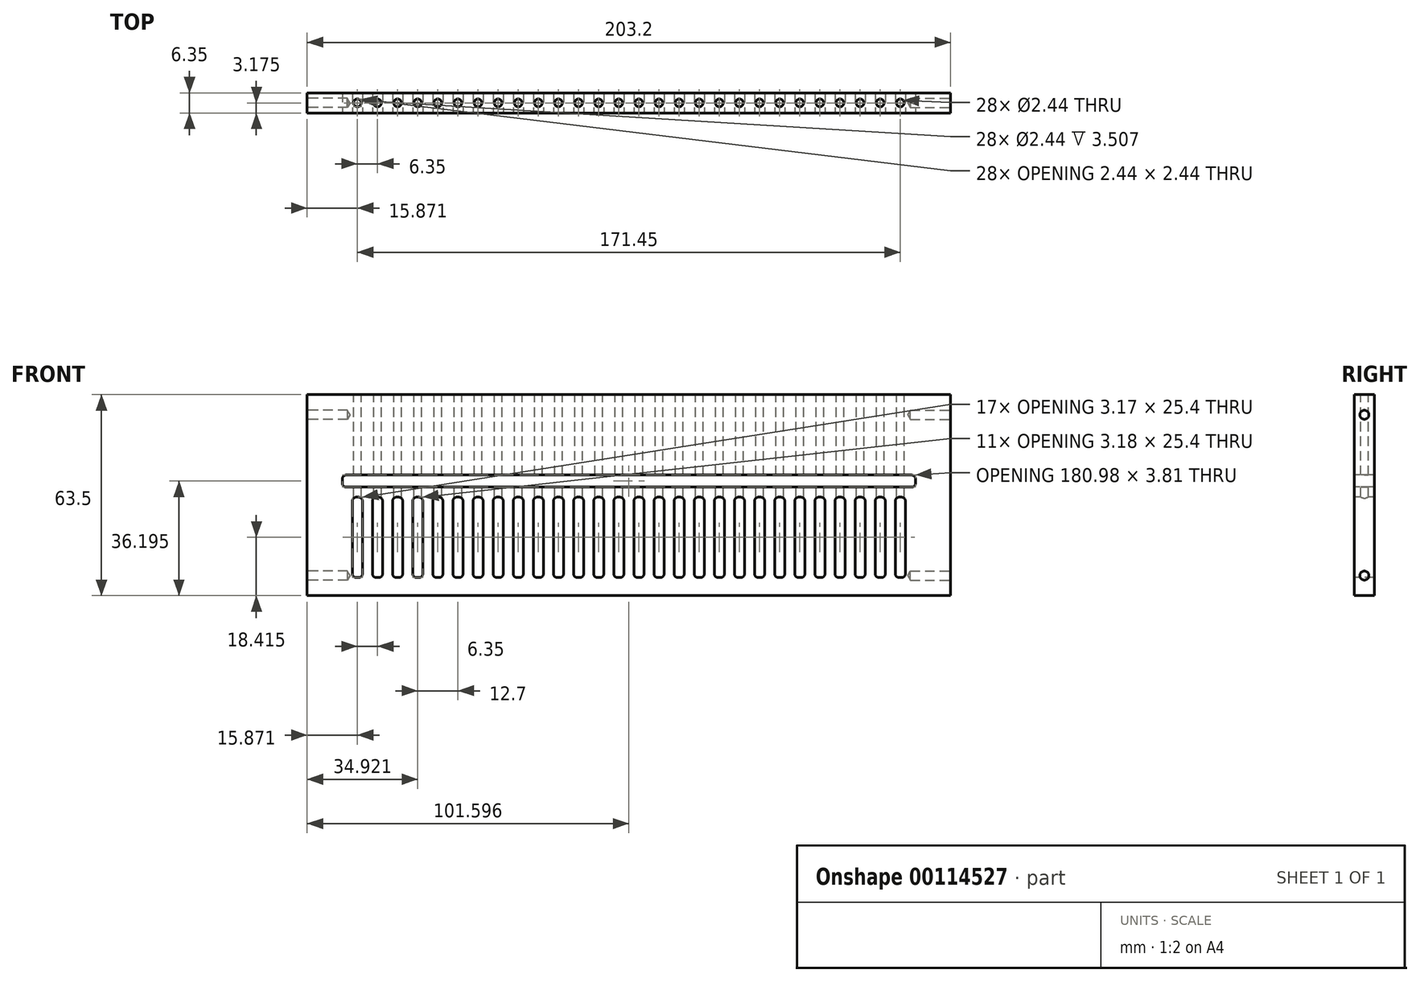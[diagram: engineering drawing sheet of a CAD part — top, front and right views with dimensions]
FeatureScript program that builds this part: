
annotation { "Feature Type Name" : "Feature", "Feature Type Description" : "" }
export const myFeature = defineFeature(function(context is Context, id is Id, definition is map)
    precondition{}
    {
        {
            var Q0;
            Q0=qCreatedBy(makeId("Top.planeOp"),FACE);
            var sketch = newSketch(context, id + "F0", { "sketchPlane" : qUnion([Q0])});
            skLineSegment(sketch, "E0.bottom", {"start": v(-24.78, 0) * mm, "end": v(178.42, 0) * mm});
            skLineSegment(sketch, "E0.top", {"start": v(-24.78, 6.35) * mm, "end": v(178.42, 6.35) * mm});
            skLineSegment(sketch, "E0.left", {"start": v(-24.78, 0) * mm, "end": v(-24.78, 6.35) * mm});
            skLineSegment(sketch, "E0.right", {"start": v(178.42, 0) * mm, "end": v(178.42, 6.35) * mm});
            skSolve(sketch);
        }
        {
            var Q0;
            Q0 = qSketchRegion(id + "F0", true);
            extrude(context, id + "F1", {"entities" : qUnion([Q0]), "depth" : 63.5 * mm});
        }
        {
            var Q0;
            Q0=makeQuery(id+"F1.opExtrude","CAP_FACE",FACE,{"disambiguationData":[OSD([sQuery(id+"F0.wireOp",EDGE,"E0.bottom"),sQuery(id+"F0.wireOp",EDGE,"E0.top"),sQuery(id+"F0.wireOp",EDGE,"E0.left"),sQuery(id+"F0.wireOp",EDGE,"E0.right")])],"isStart":false});
            var sketch = newSketch(context, id + "F2", { "sketchPlane" : qUnion([Q0])});
            skCircle(sketch, "E1", {"center": v(-8.9, 3.18) * mm, "radius": 1.22 * mm});
            skCircle(sketch, "E2.1.0.0", {"center": v(-2.56, 3.18) * mm, "radius": 1.22 * mm});
            skCircle(sketch, "E2.2.0.0", {"center": v(3.8, 3.18) * mm, "radius": 1.22 * mm});
            skCircle(sketch, "E2.3.0.0", {"center": v(10.14, 3.18) * mm, "radius": 1.22 * mm});
            skCircle(sketch, "E2.4.0.0", {"center": v(16.5, 3.18) * mm, "radius": 1.22 * mm});
            skCircle(sketch, "E2.5.0.0", {"center": v(22.84, 3.18) * mm, "radius": 1.22 * mm});
            skCircle(sketch, "E2.6.0.0", {"center": v(29.2, 3.18) * mm, "radius": 1.22 * mm});
            skCircle(sketch, "E2.7.0.0", {"center": v(35.54, 3.18) * mm, "radius": 1.22 * mm});
            skCircle(sketch, "E2.8.0.0", {"center": v(41.9, 3.18) * mm, "radius": 1.22 * mm});
            skCircle(sketch, "E2.9.0.0", {"center": v(48.24, 3.18) * mm, "radius": 1.22 * mm});
            skCircle(sketch, "E2.10.0.0", {"center": v(54.6, 3.18) * mm, "radius": 1.22 * mm});
            skCircle(sketch, "E2.11.0.0", {"center": v(60.94, 3.18) * mm, "radius": 1.22 * mm});
            skCircle(sketch, "E2.12.0.0", {"center": v(67.3, 3.18) * mm, "radius": 1.22 * mm});
            skCircle(sketch, "E2.13.0.0", {"center": v(73.64, 3.18) * mm, "radius": 1.22 * mm});
            skCircle(sketch, "E2.14.0.0", {"center": v(80, 3.18) * mm, "radius": 1.22 * mm});
            skCircle(sketch, "E2.15.0.0", {"center": v(86.34, 3.18) * mm, "radius": 1.22 * mm});
            skCircle(sketch, "E2.16.0.0", {"center": v(92.7, 3.18) * mm, "radius": 1.22 * mm});
            skCircle(sketch, "E2.17.0.0", {"center": v(99.04, 3.18) * mm, "radius": 1.22 * mm});
            skCircle(sketch, "E2.18.0.0", {"center": v(105.4, 3.18) * mm, "radius": 1.22 * mm});
            skCircle(sketch, "E2.19.0.0", {"center": v(111.74, 3.18) * mm, "radius": 1.22 * mm});
            skCircle(sketch, "E2.20.0.0", {"center": v(118.1, 3.18) * mm, "radius": 1.22 * mm});
            skCircle(sketch, "E2.21.0.0", {"center": v(124.44, 3.18) * mm, "radius": 1.22 * mm});
            skCircle(sketch, "E2.22.0.0", {"center": v(130.8, 3.18) * mm, "radius": 1.22 * mm});
            skCircle(sketch, "E2.23.0.0", {"center": v(137.14, 3.18) * mm, "radius": 1.22 * mm});
            skCircle(sketch, "E2.24.0.0", {"center": v(143.5, 3.18) * mm, "radius": 1.22 * mm});
            skCircle(sketch, "E2.25.0.0", {"center": v(149.84, 3.18) * mm, "radius": 1.22 * mm});
            skCircle(sketch, "E2.26.0.0", {"center": v(156.2, 3.18) * mm, "radius": 1.22 * mm});
            skCircle(sketch, "E2.27.0.0", {"center": v(162.54, 3.18) * mm, "radius": 1.22 * mm});
            skLineSegment(sketch, "E2.direction1", {"start": v(-8.9, 3.18) * mm, "end": v(-2.56, 3.18) * mm, "construction": true});
            skSolve(sketch);
        }
        {
            var Q0;
            Q0 = qSketchRegion(id + "F2", true);
            extrude(context, id + "F3", {"entities" : qUnion([Q0]), "operationType" : NewBodyOperationType.REMOVE, "oppositeDirection" : true, "depth" : 38.1 * mm});
        }
        {
            var Q0;
            Q0=makeQuery(id+"F1.opExtrude","SWEPT_FACE",FACE,{"disambiguationData":[OSD([sQuery(id+"F0.wireOp",EDGE,"E0.bottom")])]});
            var sketch = newSketch(context, id + "F4", { "sketchPlane" : qUnion([Q0])});
            skLineSegment(sketch, "E3.bottom", {"start": v(-12.48, 38.1) * mm, "end": v(166.11, 38.1) * mm});
            skLineSegment(sketch, "E3.top", {"start": v(-12.48, 34.29) * mm, "end": v(166.11, 34.29) * mm});
            skLineSegment(sketch, "E3.left", {"start": v(-13.67, 36.9) * mm, "end": v(-13.67, 35.48) * mm});
            skLineSegment(sketch, "E3.right", {"start": v(167.3, 36.9) * mm, "end": v(167.3, 35.48) * mm});
            skPoint(sketch, "E4.visualSharp", {"position": v(-13.67, 38.1) * mm});
            skArc(sketch, "E4.filletArc", {"start": v(-12.48, 38.1) * mm, "mid": v(-13.32, 37.75) * mm, "end": v(-13.67, 36.9) * mm});
            skPoint(sketch, "E5.visualSharp", {"position": v(-13.67, 34.29) * mm});
            skArc(sketch, "E5.filletArc", {"start": v(-13.67, 35.48) * mm, "mid": v(-13.32, 34.64) * mm, "end": v(-12.48, 34.3) * mm});
            skPoint(sketch, "E6.visualSharp", {"position": v(167.3, 38.1) * mm});
            skArc(sketch, "E6.filletArc", {"start": v(167.3, 36.9) * mm, "mid": v(166.95, 37.75) * mm, "end": v(166.11, 38.1) * mm});
            skPoint(sketch, "E7.visualSharp", {"position": v(167.3, 34.29) * mm});
            skArc(sketch, "E7.filletArc", {"start": v(166.11, 34.29) * mm, "mid": v(166.95, 34.64) * mm, "end": v(167.3, 35.48) * mm});
            skLineSegment(sketch, "E8.bottom", {"start": v(-9.3, 31.12) * mm, "end": v(-8.51, 31.12) * mm});
            skLineSegment(sketch, "E8.top", {"start": v(-9.3, 5.71) * mm, "end": v(-8.51, 5.71) * mm});
            skLineSegment(sketch, "E8.left", {"start": v(-10.5, 29.92) * mm, "end": v(-10.5, 6.9) * mm});
            skLineSegment(sketch, "E8.right", {"start": v(-7.32, 29.92) * mm, "end": v(-7.32, 6.9) * mm});
            skPoint(sketch, "E9.visualSharp", {"position": v(-10.5, 31.12) * mm});
            skArc(sketch, "E9.filletArc", {"start": v(-9.3, 31.12) * mm, "mid": v(-10.15, 30.77) * mm, "end": v(-10.5, 29.92) * mm});
            skPoint(sketch, "E10.visualSharp", {"position": v(-7.32, 31.12) * mm});
            skArc(sketch, "E10.filletArc", {"start": v(-7.32, 29.92) * mm, "mid": v(-7.67, 30.77) * mm, "end": v(-8.51, 31.12) * mm});
            skPoint(sketch, "E11.visualSharp", {"position": v(-10.5, 5.71) * mm});
            skArc(sketch, "E11.filletArc", {"start": v(-10.5, 6.9) * mm, "mid": v(-10.15, 6.06) * mm, "end": v(-9.3, 5.71) * mm});
            skPoint(sketch, "E12.visualSharp", {"position": v(-7.32, 5.71) * mm});
            skArc(sketch, "E12.filletArc", {"start": v(-8.51, 5.71) * mm, "mid": v(-7.67, 6.06) * mm, "end": v(-7.32, 6.9) * mm});
            skPoint(sketch, "E13.1.0.0", {"position": v(-0.97, 31.12) * mm});
            skPoint(sketch, "E13.1.0.1", {"position": v(-4.15, 5.71) * mm});
            skPoint(sketch, "E13.1.0.2", {"position": v(-4.15, 31.12) * mm});
            skPoint(sketch, "E13.1.0.3", {"position": v(-0.97, 5.71) * mm});
            skLineSegment(sketch, "E13.1.0.4", {"start": v(-0.97, 29.92) * mm, "end": v(-0.97, 6.9) * mm});
            skLineSegment(sketch, "E13.1.0.5", {"start": v(-4.15, 29.92) * mm, "end": v(-4.15, 6.9) * mm});
            skArc(sketch, "E13.1.0.6", {"start": v(-2.96, 31.12) * mm, "mid": v(-3.8, 30.77) * mm, "end": v(-4.15, 29.92) * mm});
            skArc(sketch, "E13.1.0.7", {"start": v(-0.97, 29.92) * mm, "mid": v(-1.32, 30.77) * mm, "end": v(-2.16, 31.12) * mm});
            skArc(sketch, "E13.1.0.8", {"start": v(-4.15, 6.9) * mm, "mid": v(-3.8, 6.06) * mm, "end": v(-2.96, 5.71) * mm});
            skArc(sketch, "E13.1.0.9", {"start": v(-2.16, 5.71) * mm, "mid": v(-1.32, 6.06) * mm, "end": v(-0.97, 6.9) * mm});
            skLineSegment(sketch, "E13.1.0.10", {"start": v(-2.96, 5.71) * mm, "end": v(-2.16, 5.71) * mm});
            skLineSegment(sketch, "E13.1.0.11", {"start": v(-2.96, 31.12) * mm, "end": v(-2.16, 31.12) * mm});
            skPoint(sketch, "E13.2.0.0", {"position": v(5.38, 31.12) * mm});
            skPoint(sketch, "E13.2.0.1", {"position": v(2.2, 5.71) * mm});
            skPoint(sketch, "E13.2.0.2", {"position": v(2.2, 31.12) * mm});
            skPoint(sketch, "E13.2.0.3", {"position": v(5.38, 5.71) * mm});
            skLineSegment(sketch, "E13.2.0.4", {"start": v(5.38, 29.92) * mm, "end": v(5.38, 6.9) * mm});
            skLineSegment(sketch, "E13.2.0.5", {"start": v(2.2, 29.92) * mm, "end": v(2.2, 6.9) * mm});
            skArc(sketch, "E13.2.0.6", {"start": v(3.4, 31.12) * mm, "mid": v(2.55, 30.77) * mm, "end": v(2.2, 29.92) * mm});
            skArc(sketch, "E13.2.0.7", {"start": v(5.38, 29.92) * mm, "mid": v(5.03, 30.77) * mm, "end": v(4.19, 31.12) * mm});
            skArc(sketch, "E13.2.0.8", {"start": v(2.2, 6.9) * mm, "mid": v(2.55, 6.06) * mm, "end": v(3.4, 5.71) * mm});
            skArc(sketch, "E13.2.0.9", {"start": v(4.19, 5.71) * mm, "mid": v(5.03, 6.06) * mm, "end": v(5.38, 6.9) * mm});
            skLineSegment(sketch, "E13.2.0.10", {"start": v(3.4, 5.71) * mm, "end": v(4.19, 5.71) * mm});
            skLineSegment(sketch, "E13.2.0.11", {"start": v(3.4, 31.12) * mm, "end": v(4.19, 31.12) * mm});
            skPoint(sketch, "E13.3.0.0", {"position": v(11.73, 31.12) * mm});
            skPoint(sketch, "E13.3.0.1", {"position": v(8.55, 5.71) * mm});
            skPoint(sketch, "E13.3.0.2", {"position": v(8.55, 31.12) * mm});
            skPoint(sketch, "E13.3.0.3", {"position": v(11.73, 5.71) * mm});
            skLineSegment(sketch, "E13.3.0.4", {"start": v(11.73, 29.92) * mm, "end": v(11.73, 6.9) * mm});
            skLineSegment(sketch, "E13.3.0.5", {"start": v(8.55, 29.92) * mm, "end": v(8.55, 6.9) * mm});
            skArc(sketch, "E13.3.0.6", {"start": v(9.74, 31.12) * mm, "mid": v(8.9, 30.77) * mm, "end": v(8.55, 29.92) * mm});
            skArc(sketch, "E13.3.0.7", {"start": v(11.73, 29.92) * mm, "mid": v(11.38, 30.77) * mm, "end": v(10.54, 31.12) * mm});
            skArc(sketch, "E13.3.0.8", {"start": v(8.55, 6.9) * mm, "mid": v(8.9, 6.06) * mm, "end": v(9.74, 5.71) * mm});
            skArc(sketch, "E13.3.0.9", {"start": v(10.54, 5.71) * mm, "mid": v(11.38, 6.06) * mm, "end": v(11.73, 6.9) * mm});
            skLineSegment(sketch, "E13.3.0.10", {"start": v(9.74, 5.71) * mm, "end": v(10.54, 5.71) * mm});
            skLineSegment(sketch, "E13.3.0.11", {"start": v(9.74, 31.11) * mm, "end": v(10.54, 31.11) * mm});
            skPoint(sketch, "E13.4.0.0", {"position": v(18.08, 31.12) * mm});
            skPoint(sketch, "E13.4.0.1", {"position": v(14.9, 5.71) * mm});
            skPoint(sketch, "E13.4.0.2", {"position": v(14.9, 31.12) * mm});
            skPoint(sketch, "E13.4.0.3", {"position": v(18.08, 5.71) * mm});
            skLineSegment(sketch, "E13.4.0.4", {"start": v(18.08, 29.92) * mm, "end": v(18.08, 6.9) * mm});
            skLineSegment(sketch, "E13.4.0.5", {"start": v(14.9, 29.92) * mm, "end": v(14.9, 6.9) * mm});
            skArc(sketch, "E13.4.0.6", {"start": v(16.1, 31.12) * mm, "mid": v(15.25, 30.77) * mm, "end": v(14.9, 29.92) * mm});
            skArc(sketch, "E13.4.0.7", {"start": v(18.08, 29.92) * mm, "mid": v(17.73, 30.77) * mm, "end": v(16.89, 31.12) * mm});
            skArc(sketch, "E13.4.0.8", {"start": v(14.9, 6.9) * mm, "mid": v(15.25, 6.06) * mm, "end": v(16.1, 5.71) * mm});
            skArc(sketch, "E13.4.0.9", {"start": v(16.89, 5.71) * mm, "mid": v(17.73, 6.06) * mm, "end": v(18.08, 6.9) * mm});
            skLineSegment(sketch, "E13.4.0.10", {"start": v(16.1, 5.71) * mm, "end": v(16.89, 5.71) * mm});
            skLineSegment(sketch, "E13.4.0.11", {"start": v(16.1, 31.11) * mm, "end": v(16.89, 31.11) * mm});
            skPoint(sketch, "E13.5.0.0", {"position": v(24.43, 31.12) * mm});
            skPoint(sketch, "E13.5.0.1", {"position": v(21.25, 5.71) * mm});
            skPoint(sketch, "E13.5.0.2", {"position": v(21.25, 31.12) * mm});
            skPoint(sketch, "E13.5.0.3", {"position": v(24.43, 5.71) * mm});
            skLineSegment(sketch, "E13.5.0.4", {"start": v(24.43, 29.92) * mm, "end": v(24.43, 6.9) * mm});
            skLineSegment(sketch, "E13.5.0.5", {"start": v(21.25, 29.92) * mm, "end": v(21.25, 6.9) * mm});
            skArc(sketch, "E13.5.0.6", {"start": v(22.44, 31.12) * mm, "mid": v(21.6, 30.77) * mm, "end": v(21.25, 29.92) * mm});
            skArc(sketch, "E13.5.0.7", {"start": v(24.43, 29.92) * mm, "mid": v(24.08, 30.77) * mm, "end": v(23.24, 31.12) * mm});
            skArc(sketch, "E13.5.0.8", {"start": v(21.25, 6.9) * mm, "mid": v(21.6, 6.06) * mm, "end": v(22.44, 5.71) * mm});
            skArc(sketch, "E13.5.0.9", {"start": v(23.24, 5.71) * mm, "mid": v(24.08, 6.06) * mm, "end": v(24.43, 6.9) * mm});
            skLineSegment(sketch, "E13.5.0.10", {"start": v(22.44, 5.71) * mm, "end": v(23.24, 5.71) * mm});
            skLineSegment(sketch, "E13.5.0.11", {"start": v(22.44, 31.11) * mm, "end": v(23.24, 31.11) * mm});
            skPoint(sketch, "E13.6.0.0", {"position": v(30.78, 31.12) * mm});
            skPoint(sketch, "E13.6.0.1", {"position": v(27.6, 5.71) * mm});
            skPoint(sketch, "E13.6.0.2", {"position": v(27.6, 31.12) * mm});
            skPoint(sketch, "E13.6.0.3", {"position": v(30.78, 5.71) * mm});
            skLineSegment(sketch, "E13.6.0.4", {"start": v(30.78, 29.92) * mm, "end": v(30.78, 6.9) * mm});
            skLineSegment(sketch, "E13.6.0.5", {"start": v(27.6, 29.92) * mm, "end": v(27.6, 6.9) * mm});
            skArc(sketch, "E13.6.0.6", {"start": v(28.8, 31.12) * mm, "mid": v(27.95, 30.77) * mm, "end": v(27.6, 29.92) * mm});
            skArc(sketch, "E13.6.0.7", {"start": v(30.78, 29.92) * mm, "mid": v(30.43, 30.77) * mm, "end": v(29.59, 31.12) * mm});
            skArc(sketch, "E13.6.0.8", {"start": v(27.6, 6.9) * mm, "mid": v(27.95, 6.06) * mm, "end": v(28.8, 5.71) * mm});
            skArc(sketch, "E13.6.0.9", {"start": v(29.59, 5.71) * mm, "mid": v(30.43, 6.06) * mm, "end": v(30.78, 6.9) * mm});
            skLineSegment(sketch, "E13.6.0.10", {"start": v(28.8, 5.71) * mm, "end": v(29.59, 5.71) * mm});
            skLineSegment(sketch, "E13.6.0.11", {"start": v(28.8, 31.11) * mm, "end": v(29.59, 31.11) * mm});
            skPoint(sketch, "E13.7.0.0", {"position": v(37.13, 31.12) * mm});
            skPoint(sketch, "E13.7.0.1", {"position": v(33.95, 5.71) * mm});
            skPoint(sketch, "E13.7.0.2", {"position": v(33.95, 31.12) * mm});
            skPoint(sketch, "E13.7.0.3", {"position": v(37.13, 5.71) * mm});
            skLineSegment(sketch, "E13.7.0.4", {"start": v(37.13, 29.92) * mm, "end": v(37.13, 6.9) * mm});
            skLineSegment(sketch, "E13.7.0.5", {"start": v(33.95, 29.92) * mm, "end": v(33.95, 6.9) * mm});
            skArc(sketch, "E13.7.0.6", {"start": v(35.14, 31.12) * mm, "mid": v(34.3, 30.77) * mm, "end": v(33.95, 29.92) * mm});
            skArc(sketch, "E13.7.0.7", {"start": v(37.13, 29.92) * mm, "mid": v(36.78, 30.77) * mm, "end": v(35.94, 31.12) * mm});
            skArc(sketch, "E13.7.0.8", {"start": v(33.95, 6.9) * mm, "mid": v(34.3, 6.06) * mm, "end": v(35.14, 5.71) * mm});
            skArc(sketch, "E13.7.0.9", {"start": v(35.94, 5.71) * mm, "mid": v(36.78, 6.06) * mm, "end": v(37.13, 6.9) * mm});
            skLineSegment(sketch, "E13.7.0.10", {"start": v(35.14, 5.71) * mm, "end": v(35.94, 5.71) * mm});
            skLineSegment(sketch, "E13.7.0.11", {"start": v(35.14, 31.11) * mm, "end": v(35.94, 31.11) * mm});
            skPoint(sketch, "E13.8.0.0", {"position": v(43.48, 31.12) * mm});
            skPoint(sketch, "E13.8.0.1", {"position": v(40.3, 5.71) * mm});
            skPoint(sketch, "E13.8.0.2", {"position": v(40.3, 31.12) * mm});
            skPoint(sketch, "E13.8.0.3", {"position": v(43.48, 5.71) * mm});
            skLineSegment(sketch, "E13.8.0.4", {"start": v(43.48, 29.92) * mm, "end": v(43.48, 6.9) * mm});
            skLineSegment(sketch, "E13.8.0.5", {"start": v(40.3, 29.92) * mm, "end": v(40.3, 6.9) * mm});
            skArc(sketch, "E13.8.0.6", {"start": v(41.5, 31.12) * mm, "mid": v(40.65, 30.77) * mm, "end": v(40.3, 29.92) * mm});
            skArc(sketch, "E13.8.0.7", {"start": v(43.48, 29.92) * mm, "mid": v(43.13, 30.77) * mm, "end": v(42.29, 31.12) * mm});
            skArc(sketch, "E13.8.0.8", {"start": v(40.3, 6.9) * mm, "mid": v(40.65, 6.06) * mm, "end": v(41.5, 5.71) * mm});
            skArc(sketch, "E13.8.0.9", {"start": v(42.29, 5.71) * mm, "mid": v(43.13, 6.06) * mm, "end": v(43.48, 6.9) * mm});
            skLineSegment(sketch, "E13.8.0.10", {"start": v(41.5, 5.71) * mm, "end": v(42.29, 5.71) * mm});
            skLineSegment(sketch, "E13.8.0.11", {"start": v(41.5, 31.11) * mm, "end": v(42.29, 31.11) * mm});
            skPoint(sketch, "E13.9.0.0", {"position": v(49.83, 31.12) * mm});
            skPoint(sketch, "E13.9.0.1", {"position": v(46.65, 5.71) * mm});
            skPoint(sketch, "E13.9.0.2", {"position": v(46.65, 31.12) * mm});
            skPoint(sketch, "E13.9.0.3", {"position": v(49.83, 5.71) * mm});
            skLineSegment(sketch, "E13.9.0.4", {"start": v(49.83, 29.92) * mm, "end": v(49.83, 6.9) * mm});
            skLineSegment(sketch, "E13.9.0.5", {"start": v(46.65, 29.92) * mm, "end": v(46.65, 6.9) * mm});
            skArc(sketch, "E13.9.0.6", {"start": v(47.84, 31.12) * mm, "mid": v(47, 30.77) * mm, "end": v(46.65, 29.92) * mm});
            skArc(sketch, "E13.9.0.7", {"start": v(49.83, 29.92) * mm, "mid": v(49.48, 30.77) * mm, "end": v(48.64, 31.12) * mm});
            skArc(sketch, "E13.9.0.8", {"start": v(46.65, 6.9) * mm, "mid": v(47, 6.06) * mm, "end": v(47.84, 5.71) * mm});
            skArc(sketch, "E13.9.0.9", {"start": v(48.64, 5.71) * mm, "mid": v(49.48, 6.06) * mm, "end": v(49.83, 6.9) * mm});
            skLineSegment(sketch, "E13.9.0.10", {"start": v(47.84, 5.71) * mm, "end": v(48.64, 5.71) * mm});
            skLineSegment(sketch, "E13.9.0.11", {"start": v(47.84, 31.11) * mm, "end": v(48.64, 31.11) * mm});
            skPoint(sketch, "E13.10.0.0", {"position": v(56.18, 31.12) * mm});
            skPoint(sketch, "E13.10.0.1", {"position": v(53, 5.71) * mm});
            skPoint(sketch, "E13.10.0.2", {"position": v(53, 31.12) * mm});
            skPoint(sketch, "E13.10.0.3", {"position": v(56.18, 5.71) * mm});
            skLineSegment(sketch, "E13.10.0.4", {"start": v(56.18, 29.92) * mm, "end": v(56.18, 6.9) * mm});
            skLineSegment(sketch, "E13.10.0.5", {"start": v(53, 29.92) * mm, "end": v(53, 6.9) * mm});
            skArc(sketch, "E13.10.0.6", {"start": v(54.2, 31.12) * mm, "mid": v(53.35, 30.77) * mm, "end": v(53, 29.92) * mm});
            skArc(sketch, "E13.10.0.7", {"start": v(56.18, 29.92) * mm, "mid": v(55.83, 30.77) * mm, "end": v(54.99, 31.12) * mm});
            skArc(sketch, "E13.10.0.8", {"start": v(53, 6.9) * mm, "mid": v(53.35, 6.06) * mm, "end": v(54.2, 5.71) * mm});
            skArc(sketch, "E13.10.0.9", {"start": v(54.99, 5.71) * mm, "mid": v(55.83, 6.06) * mm, "end": v(56.18, 6.9) * mm});
            skLineSegment(sketch, "E13.10.0.10", {"start": v(54.2, 5.71) * mm, "end": v(54.99, 5.71) * mm});
            skLineSegment(sketch, "E13.10.0.11", {"start": v(54.2, 31.11) * mm, "end": v(54.99, 31.11) * mm});
            skPoint(sketch, "E13.11.0.0", {"position": v(62.53, 31.12) * mm});
            skPoint(sketch, "E13.11.0.1", {"position": v(59.35, 5.71) * mm});
            skPoint(sketch, "E13.11.0.2", {"position": v(59.35, 31.12) * mm});
            skPoint(sketch, "E13.11.0.3", {"position": v(62.53, 5.71) * mm});
            skLineSegment(sketch, "E13.11.0.4", {"start": v(62.53, 29.92) * mm, "end": v(62.53, 6.9) * mm});
            skLineSegment(sketch, "E13.11.0.5", {"start": v(59.35, 29.92) * mm, "end": v(59.35, 6.9) * mm});
            skArc(sketch, "E13.11.0.6", {"start": v(60.54, 31.12) * mm, "mid": v(59.7, 30.77) * mm, "end": v(59.35, 29.92) * mm});
            skArc(sketch, "E13.11.0.7", {"start": v(62.53, 29.92) * mm, "mid": v(62.18, 30.77) * mm, "end": v(61.34, 31.12) * mm});
            skArc(sketch, "E13.11.0.8", {"start": v(59.35, 6.9) * mm, "mid": v(59.7, 6.06) * mm, "end": v(60.54, 5.71) * mm});
            skArc(sketch, "E13.11.0.9", {"start": v(61.34, 5.71) * mm, "mid": v(62.18, 6.06) * mm, "end": v(62.53, 6.9) * mm});
            skLineSegment(sketch, "E13.11.0.10", {"start": v(60.54, 5.71) * mm, "end": v(61.34, 5.71) * mm});
            skLineSegment(sketch, "E13.11.0.11", {"start": v(60.54, 31.11) * mm, "end": v(61.34, 31.11) * mm});
            skPoint(sketch, "E13.12.0.0", {"position": v(68.88, 31.12) * mm});
            skPoint(sketch, "E13.12.0.1", {"position": v(65.7, 5.71) * mm});
            skPoint(sketch, "E13.12.0.2", {"position": v(65.7, 31.12) * mm});
            skPoint(sketch, "E13.12.0.3", {"position": v(68.88, 5.71) * mm});
            skLineSegment(sketch, "E13.12.0.4", {"start": v(68.88, 29.92) * mm, "end": v(68.88, 6.9) * mm});
            skLineSegment(sketch, "E13.12.0.5", {"start": v(65.7, 29.92) * mm, "end": v(65.7, 6.9) * mm});
            skArc(sketch, "E13.12.0.6", {"start": v(66.9, 31.12) * mm, "mid": v(66.05, 30.77) * mm, "end": v(65.7, 29.92) * mm});
            skArc(sketch, "E13.12.0.7", {"start": v(68.88, 29.92) * mm, "mid": v(68.53, 30.77) * mm, "end": v(67.69, 31.12) * mm});
            skArc(sketch, "E13.12.0.8", {"start": v(65.7, 6.9) * mm, "mid": v(66.05, 6.06) * mm, "end": v(66.9, 5.71) * mm});
            skArc(sketch, "E13.12.0.9", {"start": v(67.69, 5.71) * mm, "mid": v(68.53, 6.06) * mm, "end": v(68.88, 6.9) * mm});
            skLineSegment(sketch, "E13.12.0.10", {"start": v(66.9, 5.71) * mm, "end": v(67.69, 5.71) * mm});
            skLineSegment(sketch, "E13.12.0.11", {"start": v(66.9, 31.11) * mm, "end": v(67.69, 31.11) * mm});
            skPoint(sketch, "E13.13.0.0", {"position": v(75.23, 31.12) * mm});
            skPoint(sketch, "E13.13.0.1", {"position": v(72.05, 5.71) * mm});
            skPoint(sketch, "E13.13.0.2", {"position": v(72.05, 31.12) * mm});
            skPoint(sketch, "E13.13.0.3", {"position": v(75.23, 5.71) * mm});
            skLineSegment(sketch, "E13.13.0.4", {"start": v(75.23, 29.92) * mm, "end": v(75.23, 6.9) * mm});
            skLineSegment(sketch, "E13.13.0.5", {"start": v(72.05, 29.92) * mm, "end": v(72.05, 6.9) * mm});
            skArc(sketch, "E13.13.0.6", {"start": v(73.24, 31.12) * mm, "mid": v(72.4, 30.77) * mm, "end": v(72.05, 29.92) * mm});
            skArc(sketch, "E13.13.0.7", {"start": v(75.23, 29.92) * mm, "mid": v(74.88, 30.77) * mm, "end": v(74.04, 31.12) * mm});
            skArc(sketch, "E13.13.0.8", {"start": v(72.05, 6.9) * mm, "mid": v(72.4, 6.06) * mm, "end": v(73.24, 5.71) * mm});
            skArc(sketch, "E13.13.0.9", {"start": v(74.04, 5.71) * mm, "mid": v(74.88, 6.06) * mm, "end": v(75.23, 6.9) * mm});
            skLineSegment(sketch, "E13.13.0.10", {"start": v(73.24, 5.71) * mm, "end": v(74.04, 5.71) * mm});
            skLineSegment(sketch, "E13.13.0.11", {"start": v(73.24, 31.11) * mm, "end": v(74.04, 31.11) * mm});
            skPoint(sketch, "E13.14.0.0", {"position": v(81.58, 31.12) * mm});
            skPoint(sketch, "E13.14.0.1", {"position": v(78.4, 5.71) * mm});
            skPoint(sketch, "E13.14.0.2", {"position": v(78.4, 31.12) * mm});
            skPoint(sketch, "E13.14.0.3", {"position": v(81.58, 5.71) * mm});
            skLineSegment(sketch, "E13.14.0.4", {"start": v(81.58, 29.92) * mm, "end": v(81.58, 6.9) * mm});
            skLineSegment(sketch, "E13.14.0.5", {"start": v(78.4, 29.92) * mm, "end": v(78.4, 6.9) * mm});
            skArc(sketch, "E13.14.0.6", {"start": v(79.6, 31.12) * mm, "mid": v(78.75, 30.77) * mm, "end": v(78.4, 29.92) * mm});
            skArc(sketch, "E13.14.0.7", {"start": v(81.58, 29.92) * mm, "mid": v(81.23, 30.77) * mm, "end": v(80.39, 31.12) * mm});
            skArc(sketch, "E13.14.0.8", {"start": v(78.4, 6.9) * mm, "mid": v(78.75, 6.06) * mm, "end": v(79.6, 5.71) * mm});
            skArc(sketch, "E13.14.0.9", {"start": v(80.39, 5.71) * mm, "mid": v(81.23, 6.06) * mm, "end": v(81.58, 6.9) * mm});
            skLineSegment(sketch, "E13.14.0.10", {"start": v(79.6, 5.71) * mm, "end": v(80.39, 5.71) * mm});
            skLineSegment(sketch, "E13.14.0.11", {"start": v(79.6, 31.11) * mm, "end": v(80.39, 31.11) * mm});
            skPoint(sketch, "E13.15.0.0", {"position": v(87.93, 31.12) * mm});
            skPoint(sketch, "E13.15.0.1", {"position": v(84.75, 5.71) * mm});
            skPoint(sketch, "E13.15.0.2", {"position": v(84.75, 31.12) * mm});
            skPoint(sketch, "E13.15.0.3", {"position": v(87.93, 5.71) * mm});
            skLineSegment(sketch, "E13.15.0.4", {"start": v(87.93, 29.92) * mm, "end": v(87.93, 6.9) * mm});
            skLineSegment(sketch, "E13.15.0.5", {"start": v(84.75, 29.92) * mm, "end": v(84.75, 6.9) * mm});
            skArc(sketch, "E13.15.0.6", {"start": v(85.94, 31.12) * mm, "mid": v(85.1, 30.77) * mm, "end": v(84.75, 29.92) * mm});
            skArc(sketch, "E13.15.0.7", {"start": v(87.93, 29.92) * mm, "mid": v(87.58, 30.77) * mm, "end": v(86.74, 31.12) * mm});
            skArc(sketch, "E13.15.0.8", {"start": v(84.75, 6.9) * mm, "mid": v(85.1, 6.06) * mm, "end": v(85.94, 5.71) * mm});
            skArc(sketch, "E13.15.0.9", {"start": v(86.74, 5.71) * mm, "mid": v(87.58, 6.06) * mm, "end": v(87.93, 6.9) * mm});
            skLineSegment(sketch, "E13.15.0.10", {"start": v(85.94, 5.71) * mm, "end": v(86.74, 5.71) * mm});
            skLineSegment(sketch, "E13.15.0.11", {"start": v(85.94, 31.11) * mm, "end": v(86.74, 31.11) * mm});
            skPoint(sketch, "E13.16.0.0", {"position": v(94.28, 31.12) * mm});
            skPoint(sketch, "E13.16.0.1", {"position": v(91.1, 5.71) * mm});
            skPoint(sketch, "E13.16.0.2", {"position": v(91.1, 31.12) * mm});
            skPoint(sketch, "E13.16.0.3", {"position": v(94.28, 5.71) * mm});
            skLineSegment(sketch, "E13.16.0.4", {"start": v(94.28, 29.92) * mm, "end": v(94.28, 6.9) * mm});
            skLineSegment(sketch, "E13.16.0.5", {"start": v(91.1, 29.92) * mm, "end": v(91.1, 6.9) * mm});
            skArc(sketch, "E13.16.0.6", {"start": v(92.3, 31.12) * mm, "mid": v(91.45, 30.77) * mm, "end": v(91.1, 29.92) * mm});
            skArc(sketch, "E13.16.0.7", {"start": v(94.28, 29.92) * mm, "mid": v(93.93, 30.77) * mm, "end": v(93.09, 31.12) * mm});
            skArc(sketch, "E13.16.0.8", {"start": v(91.1, 6.9) * mm, "mid": v(91.45, 6.06) * mm, "end": v(92.3, 5.71) * mm});
            skArc(sketch, "E13.16.0.9", {"start": v(93.09, 5.71) * mm, "mid": v(93.93, 6.06) * mm, "end": v(94.28, 6.9) * mm});
            skLineSegment(sketch, "E13.16.0.10", {"start": v(92.3, 5.71) * mm, "end": v(93.09, 5.71) * mm});
            skLineSegment(sketch, "E13.16.0.11", {"start": v(92.3, 31.11) * mm, "end": v(93.09, 31.11) * mm});
            skPoint(sketch, "E13.17.0.0", {"position": v(100.63, 31.12) * mm});
            skPoint(sketch, "E13.17.0.1", {"position": v(97.45, 5.71) * mm});
            skPoint(sketch, "E13.17.0.2", {"position": v(97.45, 31.12) * mm});
            skPoint(sketch, "E13.17.0.3", {"position": v(100.63, 5.71) * mm});
            skLineSegment(sketch, "E13.17.0.4", {"start": v(100.63, 29.92) * mm, "end": v(100.63, 6.9) * mm});
            skLineSegment(sketch, "E13.17.0.5", {"start": v(97.45, 29.92) * mm, "end": v(97.45, 6.9) * mm});
            skArc(sketch, "E13.17.0.6", {"start": v(98.64, 31.12) * mm, "mid": v(97.8, 30.77) * mm, "end": v(97.45, 29.92) * mm});
            skArc(sketch, "E13.17.0.7", {"start": v(100.63, 29.92) * mm, "mid": v(100.28, 30.77) * mm, "end": v(99.44, 31.12) * mm});
            skArc(sketch, "E13.17.0.8", {"start": v(97.45, 6.9) * mm, "mid": v(97.8, 6.06) * mm, "end": v(98.64, 5.71) * mm});
            skArc(sketch, "E13.17.0.9", {"start": v(99.44, 5.71) * mm, "mid": v(100.28, 6.06) * mm, "end": v(100.63, 6.9) * mm});
            skLineSegment(sketch, "E13.17.0.10", {"start": v(98.64, 5.71) * mm, "end": v(99.44, 5.71) * mm});
            skLineSegment(sketch, "E13.17.0.11", {"start": v(98.64, 31.11) * mm, "end": v(99.44, 31.11) * mm});
            skPoint(sketch, "E13.18.0.0", {"position": v(106.98, 31.12) * mm});
            skPoint(sketch, "E13.18.0.1", {"position": v(103.8, 5.71) * mm});
            skPoint(sketch, "E13.18.0.2", {"position": v(103.8, 31.12) * mm});
            skPoint(sketch, "E13.18.0.3", {"position": v(106.98, 5.71) * mm});
            skLineSegment(sketch, "E13.18.0.4", {"start": v(106.98, 29.92) * mm, "end": v(106.98, 6.9) * mm});
            skLineSegment(sketch, "E13.18.0.5", {"start": v(103.8, 29.92) * mm, "end": v(103.8, 6.9) * mm});
            skArc(sketch, "E13.18.0.6", {"start": v(105, 31.12) * mm, "mid": v(104.15, 30.77) * mm, "end": v(103.8, 29.92) * mm});
            skArc(sketch, "E13.18.0.7", {"start": v(106.98, 29.92) * mm, "mid": v(106.63, 30.77) * mm, "end": v(105.79, 31.12) * mm});
            skArc(sketch, "E13.18.0.8", {"start": v(103.8, 6.9) * mm, "mid": v(104.15, 6.06) * mm, "end": v(105, 5.71) * mm});
            skArc(sketch, "E13.18.0.9", {"start": v(105.79, 5.71) * mm, "mid": v(106.63, 6.06) * mm, "end": v(106.98, 6.9) * mm});
            skLineSegment(sketch, "E13.18.0.10", {"start": v(105, 5.71) * mm, "end": v(105.79, 5.71) * mm});
            skLineSegment(sketch, "E13.18.0.11", {"start": v(105, 31.11) * mm, "end": v(105.79, 31.11) * mm});
            skPoint(sketch, "E13.19.0.0", {"position": v(113.33, 31.12) * mm});
            skPoint(sketch, "E13.19.0.1", {"position": v(110.15, 5.71) * mm});
            skPoint(sketch, "E13.19.0.2", {"position": v(110.15, 31.12) * mm});
            skPoint(sketch, "E13.19.0.3", {"position": v(113.33, 5.71) * mm});
            skLineSegment(sketch, "E13.19.0.4", {"start": v(113.33, 29.92) * mm, "end": v(113.33, 6.9) * mm});
            skLineSegment(sketch, "E13.19.0.5", {"start": v(110.15, 29.92) * mm, "end": v(110.15, 6.9) * mm});
            skArc(sketch, "E13.19.0.6", {"start": v(111.34, 31.12) * mm, "mid": v(110.5, 30.77) * mm, "end": v(110.15, 29.92) * mm});
            skArc(sketch, "E13.19.0.7", {"start": v(113.33, 29.92) * mm, "mid": v(112.98, 30.77) * mm, "end": v(112.14, 31.12) * mm});
            skArc(sketch, "E13.19.0.8", {"start": v(110.15, 6.9) * mm, "mid": v(110.5, 6.06) * mm, "end": v(111.34, 5.71) * mm});
            skArc(sketch, "E13.19.0.9", {"start": v(112.14, 5.71) * mm, "mid": v(112.98, 6.06) * mm, "end": v(113.33, 6.9) * mm});
            skLineSegment(sketch, "E13.19.0.10", {"start": v(111.34, 5.71) * mm, "end": v(112.14, 5.71) * mm});
            skLineSegment(sketch, "E13.19.0.11", {"start": v(111.34, 31.11) * mm, "end": v(112.14, 31.11) * mm});
            skPoint(sketch, "E13.20.0.0", {"position": v(119.68, 31.12) * mm});
            skPoint(sketch, "E13.20.0.1", {"position": v(116.5, 5.71) * mm});
            skPoint(sketch, "E13.20.0.2", {"position": v(116.5, 31.12) * mm});
            skPoint(sketch, "E13.20.0.3", {"position": v(119.68, 5.71) * mm});
            skLineSegment(sketch, "E13.20.0.4", {"start": v(119.68, 29.92) * mm, "end": v(119.68, 6.9) * mm});
            skLineSegment(sketch, "E13.20.0.5", {"start": v(116.5, 29.92) * mm, "end": v(116.5, 6.9) * mm});
            skArc(sketch, "E13.20.0.6", {"start": v(117.7, 31.12) * mm, "mid": v(116.85, 30.77) * mm, "end": v(116.5, 29.92) * mm});
            skArc(sketch, "E13.20.0.7", {"start": v(119.68, 29.92) * mm, "mid": v(119.33, 30.77) * mm, "end": v(118.49, 31.12) * mm});
            skArc(sketch, "E13.20.0.8", {"start": v(116.5, 6.9) * mm, "mid": v(116.85, 6.06) * mm, "end": v(117.7, 5.71) * mm});
            skArc(sketch, "E13.20.0.9", {"start": v(118.49, 5.71) * mm, "mid": v(119.33, 6.06) * mm, "end": v(119.68, 6.9) * mm});
            skLineSegment(sketch, "E13.20.0.10", {"start": v(117.7, 5.71) * mm, "end": v(118.49, 5.71) * mm});
            skLineSegment(sketch, "E13.20.0.11", {"start": v(117.7, 31.11) * mm, "end": v(118.49, 31.11) * mm});
            skPoint(sketch, "E13.21.0.0", {"position": v(126.03, 31.12) * mm});
            skPoint(sketch, "E13.21.0.1", {"position": v(122.85, 5.71) * mm});
            skPoint(sketch, "E13.21.0.2", {"position": v(122.85, 31.12) * mm});
            skPoint(sketch, "E13.21.0.3", {"position": v(126.03, 5.71) * mm});
            skLineSegment(sketch, "E13.21.0.4", {"start": v(126.03, 29.92) * mm, "end": v(126.03, 6.9) * mm});
            skLineSegment(sketch, "E13.21.0.5", {"start": v(122.85, 29.92) * mm, "end": v(122.85, 6.9) * mm});
            skArc(sketch, "E13.21.0.6", {"start": v(124.04, 31.12) * mm, "mid": v(123.2, 30.77) * mm, "end": v(122.85, 29.92) * mm});
            skArc(sketch, "E13.21.0.7", {"start": v(126.03, 29.92) * mm, "mid": v(125.68, 30.77) * mm, "end": v(124.84, 31.12) * mm});
            skArc(sketch, "E13.21.0.8", {"start": v(122.85, 6.9) * mm, "mid": v(123.2, 6.06) * mm, "end": v(124.04, 5.71) * mm});
            skArc(sketch, "E13.21.0.9", {"start": v(124.84, 5.71) * mm, "mid": v(125.68, 6.06) * mm, "end": v(126.03, 6.9) * mm});
            skLineSegment(sketch, "E13.21.0.10", {"start": v(124.04, 5.71) * mm, "end": v(124.84, 5.71) * mm});
            skLineSegment(sketch, "E13.21.0.11", {"start": v(124.04, 31.11) * mm, "end": v(124.84, 31.11) * mm});
            skPoint(sketch, "E13.22.0.0", {"position": v(132.38, 31.12) * mm});
            skPoint(sketch, "E13.22.0.1", {"position": v(129.2, 5.71) * mm});
            skPoint(sketch, "E13.22.0.2", {"position": v(129.2, 31.12) * mm});
            skPoint(sketch, "E13.22.0.3", {"position": v(132.38, 5.71) * mm});
            skLineSegment(sketch, "E13.22.0.4", {"start": v(132.38, 29.92) * mm, "end": v(132.38, 6.9) * mm});
            skLineSegment(sketch, "E13.22.0.5", {"start": v(129.2, 29.92) * mm, "end": v(129.2, 6.9) * mm});
            skArc(sketch, "E13.22.0.6", {"start": v(130.4, 31.12) * mm, "mid": v(129.55, 30.77) * mm, "end": v(129.2, 29.92) * mm});
            skArc(sketch, "E13.22.0.7", {"start": v(132.38, 29.92) * mm, "mid": v(132.03, 30.77) * mm, "end": v(131.19, 31.12) * mm});
            skArc(sketch, "E13.22.0.8", {"start": v(129.2, 6.9) * mm, "mid": v(129.55, 6.06) * mm, "end": v(130.4, 5.71) * mm});
            skArc(sketch, "E13.22.0.9", {"start": v(131.19, 5.71) * mm, "mid": v(132.03, 6.06) * mm, "end": v(132.38, 6.9) * mm});
            skLineSegment(sketch, "E13.22.0.10", {"start": v(130.4, 5.71) * mm, "end": v(131.19, 5.71) * mm});
            skLineSegment(sketch, "E13.22.0.11", {"start": v(130.4, 31.11) * mm, "end": v(131.19, 31.11) * mm});
            skPoint(sketch, "E13.23.0.0", {"position": v(138.73, 31.12) * mm});
            skPoint(sketch, "E13.23.0.1", {"position": v(135.55, 5.71) * mm});
            skPoint(sketch, "E13.23.0.2", {"position": v(135.55, 31.12) * mm});
            skPoint(sketch, "E13.23.0.3", {"position": v(138.73, 5.71) * mm});
            skLineSegment(sketch, "E13.23.0.4", {"start": v(138.73, 29.92) * mm, "end": v(138.73, 6.9) * mm});
            skLineSegment(sketch, "E13.23.0.5", {"start": v(135.55, 29.92) * mm, "end": v(135.55, 6.9) * mm});
            skArc(sketch, "E13.23.0.6", {"start": v(136.74, 31.12) * mm, "mid": v(135.9, 30.77) * mm, "end": v(135.55, 29.92) * mm});
            skArc(sketch, "E13.23.0.7", {"start": v(138.73, 29.92) * mm, "mid": v(138.38, 30.77) * mm, "end": v(137.54, 31.12) * mm});
            skArc(sketch, "E13.23.0.8", {"start": v(135.55, 6.9) * mm, "mid": v(135.9, 6.06) * mm, "end": v(136.74, 5.71) * mm});
            skArc(sketch, "E13.23.0.9", {"start": v(137.54, 5.71) * mm, "mid": v(138.38, 6.06) * mm, "end": v(138.73, 6.9) * mm});
            skLineSegment(sketch, "E13.23.0.10", {"start": v(136.74, 5.71) * mm, "end": v(137.54, 5.71) * mm});
            skLineSegment(sketch, "E13.23.0.11", {"start": v(136.74, 31.11) * mm, "end": v(137.54, 31.11) * mm});
            skPoint(sketch, "E13.24.0.0", {"position": v(145.08, 31.12) * mm});
            skPoint(sketch, "E13.24.0.1", {"position": v(141.9, 5.71) * mm});
            skPoint(sketch, "E13.24.0.2", {"position": v(141.9, 31.12) * mm});
            skPoint(sketch, "E13.24.0.3", {"position": v(145.08, 5.71) * mm});
            skLineSegment(sketch, "E13.24.0.4", {"start": v(145.08, 29.92) * mm, "end": v(145.08, 6.9) * mm});
            skLineSegment(sketch, "E13.24.0.5", {"start": v(141.9, 29.92) * mm, "end": v(141.9, 6.9) * mm});
            skArc(sketch, "E13.24.0.6", {"start": v(143.1, 31.12) * mm, "mid": v(142.25, 30.77) * mm, "end": v(141.9, 29.92) * mm});
            skArc(sketch, "E13.24.0.7", {"start": v(145.08, 29.92) * mm, "mid": v(144.73, 30.77) * mm, "end": v(143.89, 31.12) * mm});
            skArc(sketch, "E13.24.0.8", {"start": v(141.9, 6.9) * mm, "mid": v(142.25, 6.06) * mm, "end": v(143.1, 5.71) * mm});
            skArc(sketch, "E13.24.0.9", {"start": v(143.89, 5.71) * mm, "mid": v(144.73, 6.06) * mm, "end": v(145.08, 6.9) * mm});
            skLineSegment(sketch, "E13.24.0.10", {"start": v(143.1, 5.71) * mm, "end": v(143.89, 5.71) * mm});
            skLineSegment(sketch, "E13.24.0.11", {"start": v(143.1, 31.11) * mm, "end": v(143.89, 31.11) * mm});
            skPoint(sketch, "E13.25.0.0", {"position": v(151.43, 31.12) * mm});
            skPoint(sketch, "E13.25.0.1", {"position": v(148.25, 5.71) * mm});
            skPoint(sketch, "E13.25.0.2", {"position": v(148.25, 31.12) * mm});
            skPoint(sketch, "E13.25.0.3", {"position": v(151.43, 5.71) * mm});
            skLineSegment(sketch, "E13.25.0.4", {"start": v(151.43, 29.92) * mm, "end": v(151.43, 6.9) * mm});
            skLineSegment(sketch, "E13.25.0.5", {"start": v(148.25, 29.92) * mm, "end": v(148.25, 6.9) * mm});
            skArc(sketch, "E13.25.0.6", {"start": v(149.44, 31.12) * mm, "mid": v(148.6, 30.77) * mm, "end": v(148.25, 29.92) * mm});
            skArc(sketch, "E13.25.0.7", {"start": v(151.43, 29.92) * mm, "mid": v(151.08, 30.77) * mm, "end": v(150.24, 31.12) * mm});
            skArc(sketch, "E13.25.0.8", {"start": v(148.25, 6.9) * mm, "mid": v(148.6, 6.06) * mm, "end": v(149.44, 5.71) * mm});
            skArc(sketch, "E13.25.0.9", {"start": v(150.24, 5.71) * mm, "mid": v(151.08, 6.06) * mm, "end": v(151.43, 6.9) * mm});
            skLineSegment(sketch, "E13.25.0.10", {"start": v(149.44, 5.71) * mm, "end": v(150.24, 5.71) * mm});
            skLineSegment(sketch, "E13.25.0.11", {"start": v(149.44, 31.11) * mm, "end": v(150.24, 31.11) * mm});
            skPoint(sketch, "E13.26.0.0", {"position": v(157.78, 31.12) * mm});
            skPoint(sketch, "E13.26.0.1", {"position": v(154.6, 5.71) * mm});
            skPoint(sketch, "E13.26.0.2", {"position": v(154.6, 31.12) * mm});
            skPoint(sketch, "E13.26.0.3", {"position": v(157.78, 5.71) * mm});
            skLineSegment(sketch, "E13.26.0.4", {"start": v(157.78, 29.92) * mm, "end": v(157.78, 6.9) * mm});
            skLineSegment(sketch, "E13.26.0.5", {"start": v(154.6, 29.92) * mm, "end": v(154.6, 6.9) * mm});
            skArc(sketch, "E13.26.0.6", {"start": v(155.8, 31.12) * mm, "mid": v(154.95, 30.77) * mm, "end": v(154.6, 29.92) * mm});
            skArc(sketch, "E13.26.0.7", {"start": v(157.78, 29.92) * mm, "mid": v(157.43, 30.77) * mm, "end": v(156.59, 31.12) * mm});
            skArc(sketch, "E13.26.0.8", {"start": v(154.6, 6.9) * mm, "mid": v(154.95, 6.06) * mm, "end": v(155.8, 5.71) * mm});
            skArc(sketch, "E13.26.0.9", {"start": v(156.59, 5.71) * mm, "mid": v(157.43, 6.06) * mm, "end": v(157.78, 6.9) * mm});
            skLineSegment(sketch, "E13.26.0.10", {"start": v(155.8, 5.71) * mm, "end": v(156.59, 5.71) * mm});
            skLineSegment(sketch, "E13.26.0.11", {"start": v(155.8, 31.11) * mm, "end": v(156.59, 31.11) * mm});
            skPoint(sketch, "E13.27.0.0", {"position": v(164.13, 31.12) * mm});
            skPoint(sketch, "E13.27.0.1", {"position": v(160.95, 5.71) * mm});
            skPoint(sketch, "E13.27.0.2", {"position": v(160.95, 31.12) * mm});
            skPoint(sketch, "E13.27.0.3", {"position": v(164.13, 5.71) * mm});
            skLineSegment(sketch, "E13.27.0.4", {"start": v(164.13, 29.92) * mm, "end": v(164.13, 6.9) * mm});
            skLineSegment(sketch, "E13.27.0.5", {"start": v(160.95, 29.92) * mm, "end": v(160.95, 6.9) * mm});
            skArc(sketch, "E13.27.0.6", {"start": v(162.14, 31.12) * mm, "mid": v(161.3, 30.77) * mm, "end": v(160.95, 29.92) * mm});
            skArc(sketch, "E13.27.0.7", {"start": v(164.13, 29.92) * mm, "mid": v(163.78, 30.77) * mm, "end": v(162.94, 31.12) * mm});
            skArc(sketch, "E13.27.0.8", {"start": v(160.95, 6.9) * mm, "mid": v(161.3, 6.06) * mm, "end": v(162.14, 5.71) * mm});
            skArc(sketch, "E13.27.0.9", {"start": v(162.94, 5.71) * mm, "mid": v(163.78, 6.06) * mm, "end": v(164.13, 6.9) * mm});
            skLineSegment(sketch, "E13.27.0.10", {"start": v(162.14, 5.71) * mm, "end": v(162.94, 5.71) * mm});
            skLineSegment(sketch, "E13.27.0.11", {"start": v(162.14, 31.11) * mm, "end": v(162.94, 31.11) * mm});
            skLineSegment(sketch, "E13.direction1", {"start": v(-10.5, 5.71) * mm, "end": v(-4.15, 5.71) * mm, "construction": true});
            skSolve(sketch);
        }
        {
            var Q0;
            Q0 = qSketchRegion(id + "F4", true);
            extrude(context, id + "F5", {"entities" : qUnion([Q0]), "operationType" : NewBodyOperationType.REMOVE, "endBound" : BoundingType.THROUGH_ALL, "oppositeDirection" : true, "depth" : 25.4 * mm});
        }
        {
            var Q0;
            Q0=makeQuery(id+"F1.opExtrude","SWEPT_FACE",FACE,{"disambiguationData":[OSD([sQuery(id+"F0.wireOp",EDGE,"E0.right")])]});
            var sketch = newSketch(context, id + "F6", { "sketchPlane" : qUnion([Q0])});
            skPoint(sketch, "E14", {"position": v(3.17, 57.15) * mm});
            skPoint(sketch, "E15", {"position": v(3.17, 6.35) * mm});
            skPoint(sketch, "E16", {"position": v(3.17, 0) * mm});
            skSolve(sketch);
        }
        {
            var Q0;
            Q0=sQuery(id+"F6.wireOp",VERTEX,"E14");
            var Q1;
            Q1=sQuery(id+"F6.wireOp",VERTEX,"E15");
            var Q2;
            Q2=makeQuery(id+"F1.opExtrude","SWEPT_BODY",BODY,{"disambiguationData":[OSD([sQuery(id+"F0.wireOp",EDGE,"E0.bottom"),sQuery(id+"F0.wireOp",EDGE,"E0.top"),sQuery(id+"F0.wireOp",EDGE,"E0.left"),sQuery(id+"F0.wireOp",EDGE,"E0.right")])]});
            hole(context, id + "F7", {"style" : HoleStyle.SIMPLE, "endStyle" : HoleEndStyle.BLIND, "standardTappedOrClearance" : lookupTablePath({ "standard" : "ANSI", "engagement" : "75%", "pitch" : "40 tpi", "size" : "#6", "type" : "Tapped" }), "standardBlindInLast" : lookupTablePath({ "standard" : "ANSI", "engagement" : "75%", "pitch" : "40 tpi", "size" : "#6", "type" : "Tapped" }), "holeDiameter" : 2.87 * mm, "holeDepth" : 12.7 * mm, "locations" : qUnion([Q0, Q1]), "scope" : qUnion([Q2]), "majorDiameter" : 3.5 * mm});
        }
        {
            var Q0;
            Q0=makeQuery(id+"F1.opExtrude","SWEPT_FACE",FACE,{"disambiguationData":[OSD([sQuery(id+"F0.wireOp",EDGE,"E0.left")])]});
            var sketch = newSketch(context, id + "F8", { "sketchPlane" : qUnion([Q0])});
            skPoint(sketch, "E17", {"position": v(-3.18, 57.15) * mm});
            skPoint(sketch, "E18", {"position": v(-3.18, 6.35) * mm});
            skSolve(sketch);
        }
        {
            var Q0;
            Q0=sQuery(id+"F8.wireOp",VERTEX,"E17");
            var Q1;
            Q1=sQuery(id+"F8.wireOp",VERTEX,"E18");
            var Q2;
            Q2=makeQuery(id+"F1.opExtrude","SWEPT_BODY",BODY,{"disambiguationData":[OSD([sQuery(id+"F0.wireOp",EDGE,"E0.bottom"),sQuery(id+"F0.wireOp",EDGE,"E0.top"),sQuery(id+"F0.wireOp",EDGE,"E0.left"),sQuery(id+"F0.wireOp",EDGE,"E0.right")])]});
            hole(context, id + "F9", {"style" : HoleStyle.SIMPLE, "endStyle" : HoleEndStyle.BLIND, "standardTappedOrClearance" : lookupTablePath({ "standard" : "ANSI", "engagement" : "75%", "pitch" : "40 tpi", "size" : "#6", "type" : "Tapped" }), "standardBlindInLast" : lookupTablePath({ "standard" : "ANSI", "engagement" : "75%", "pitch" : "40 tpi", "size" : "#6", "type" : "Tapped" }), "holeDiameter" : 2.87 * mm, "holeDepth" : 12.7 * mm, "locations" : qUnion([Q0, Q1]), "scope" : qUnion([Q2]), "majorDiameter" : 3.5 * mm});
        }
    });
